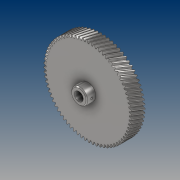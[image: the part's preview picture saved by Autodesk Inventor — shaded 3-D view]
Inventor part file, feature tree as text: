
AUTODESK INVENTOR PART (.ipt)
format: ipt  version: 2021 (Build 250183000, 183)  size: 1,273,344 bytes
history: native  units: mm (DEFAULTED — no unit token found)
features: extrude x4, sketch x4, plane x3, other x3, projected_geometry x2, chamfer x1, pattern_circular x1
ambient origin geometry x8: Origin, YZ Plane, XZ Plane, XY Plane, X Axis, Y Axis, Z Axis, Center Point
bodies: Solid1 (feature_tree)
feature tree (18):
  extrude  "Extrusion1"  Depth=15.0mm TaperAngle=0.0deg
  plane  "Work Plane2"
  plane  "Work Plane8"
  plane  "Work Plane9"
  other  "Spur Gear"
  sketch  "Sketch3"  dims[d16=59.86mm d17=0.0mm d34=0.436332mm]
  extrude  "Extrusion2"  Depth=10.0mm TaperAngle=0.0deg
  extrude  "Extrusion3"  Depth=0.436332mm TaperAngle=0.0deg
  chamfer  "Chamfer1"  [1 undecoded]
  extrude  "Extrusion4"  Depth=15.0mm
  pattern_circular  "Circular Pattern1"  [2 undecoded]
  sketch  "Sketch1"  dims[d0=98.276mm d1=15.0mm d2=0.0mm]
  sketch  "Sketch2"  dims[d3=95.776mm d4=10.0mm d5=0.0mm]
  other  "Srf1"
  projected_geometry  "Projected Loop1"
  sketch  "Sketch4"  dims[d39=0.0mm d41=0.0mm d43=59.86mm d46=59.86mm d47=0.0mm d48=0.0mm d49=10.0mm d50=4.0mm d51=22.0mm d52=0.0mm d53=10.0mm d54=0.0mm d55=1.0mm d56=2.0mm d57=45.0deg d58=2.5mm d59=15.0mm d60=0.0mm d61=20.0mm d62=90.0deg]
  projected_geometry  "Projected Loop2"
  other  "Pitch Diameter"
note: 3 required parameter values undecoded (feature->parameter linkage not recoverable at this tier; creation-order binding heuristic only, values carry confidence <= 0.55)
